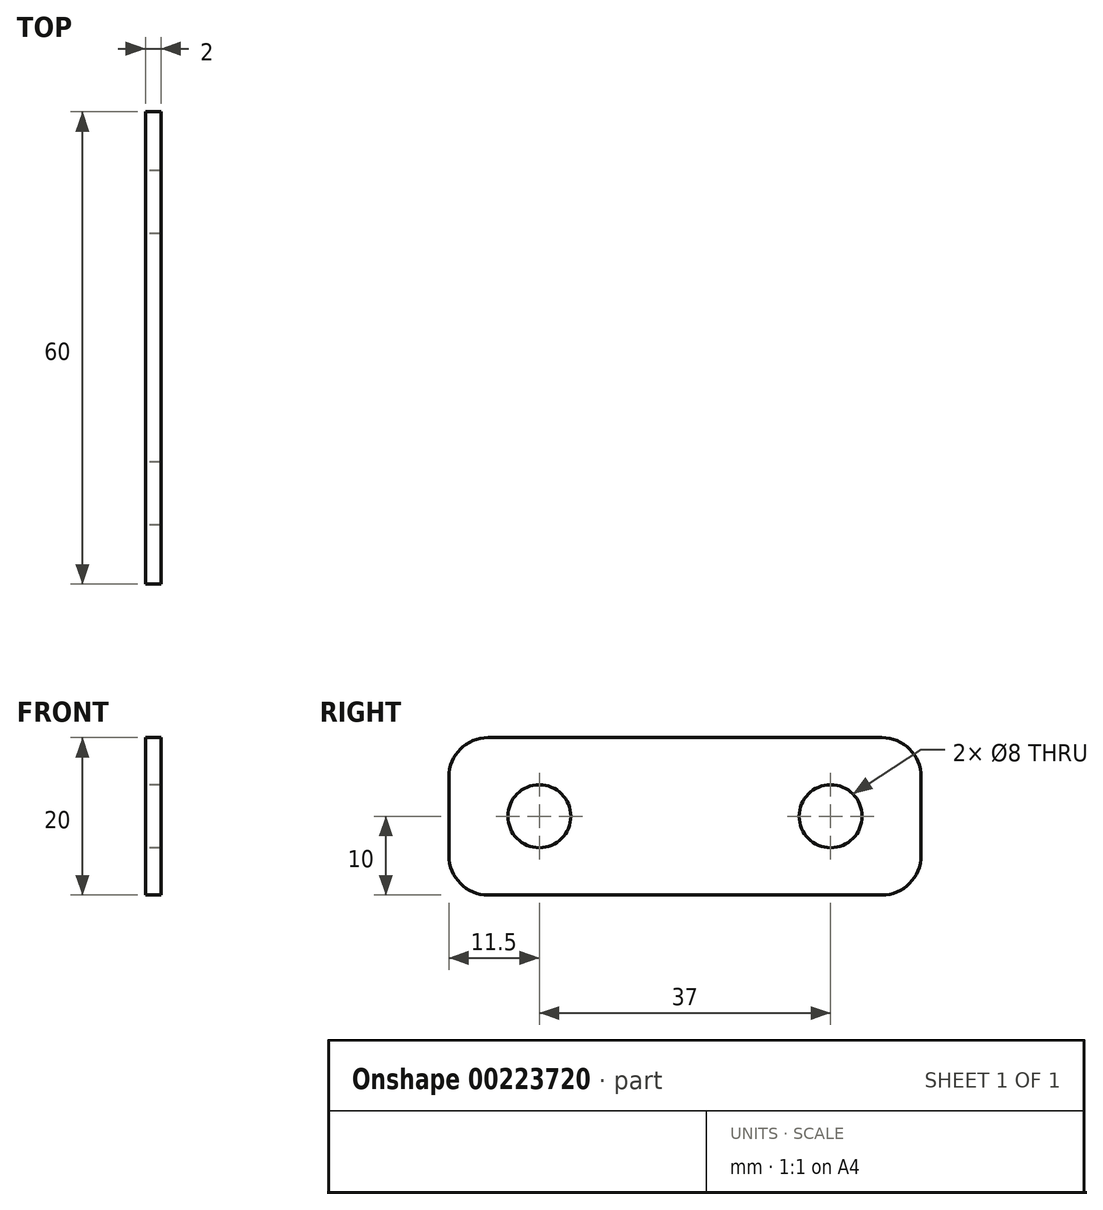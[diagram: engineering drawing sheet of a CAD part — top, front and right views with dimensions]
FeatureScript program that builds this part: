
annotation { "Feature Type Name" : "Feature", "Feature Type Description" : "" }
export const myFeature = defineFeature(function(context is Context, id is Id, definition is map)
    precondition{}
    {
        {
            var Q0;
            Q0=qCreatedBy(makeId("Right.planeOp"),FACE);
            var sketch = newSketch(context, id + "F0", { "sketchPlane" : qUnion([Q0])});
            skLineSegment(sketch, "E0.bottom", {"start": v(30, -10) * mm, "end": v(-30, -10) * mm});
            skLineSegment(sketch, "E0.top", {"start": v(30, 10) * mm, "end": v(-30, 10) * mm});
            skLineSegment(sketch, "E0.left", {"start": v(30, -10) * mm, "end": v(30, 10) * mm});
            skLineSegment(sketch, "E0.right", {"start": v(-30, -10) * mm, "end": v(-30, 10) * mm});
            skPoint(sketch, "E0.middle", {"position": v(0, 0) * mm});
            skCircle(sketch, "E1", {"center": v(-18.5, 0) * mm, "radius": 4 * mm});
            skCircle(sketch, "E2.MirrorC", {"center": v(18.5, 0) * mm, "radius": 4 * mm});
            skSolve(sketch);
        }
        {
            var Q0;
            Q0=qSketchRegion(id+"F0",true);
            extrude(context, id + "F1", {"entities" : qUnion([Q0]), "depth" : 2 * mm});
        }
        {
            var Q0;
            Q0=makeQuery(id+"F1.opExtrude","SWEPT_EDGE",EDGE,{"disambiguationData":[OSD([sQuery(id+"F0.wireOp",EDGE,"E0.top"),sQuery(id+"F0.wireOp",EDGE,"E0.right")])]});
            var Q1;
            Q1=makeQuery(id+"F1.opExtrude","SWEPT_EDGE",EDGE,{"disambiguationData":[OSD([sQuery(id+"F0.wireOp",EDGE,"E0.bottom"),sQuery(id+"F0.wireOp",EDGE,"E0.right")])]});
            var Q2;
            Q2=makeQuery(id+"F1.opExtrude","SWEPT_EDGE",EDGE,{"disambiguationData":[OSD([sQuery(id+"F0.wireOp",EDGE,"E0.top"),sQuery(id+"F0.wireOp",EDGE,"E0.left")])]});
            var Q3;
            Q3=makeQuery(id+"F1.opExtrude","SWEPT_EDGE",EDGE,{"disambiguationData":[OSD([sQuery(id+"F0.wireOp",EDGE,"E0.bottom"),sQuery(id+"F0.wireOp",EDGE,"E0.left")])]});
            fillet(context, id + "F2", {"entities" : qUnion([Q0, Q1, Q2, Q3]), "radius" : 5 * mm, "tangentPropagation" : true, "allowEdgeOverflow" : false});
        }
    });
